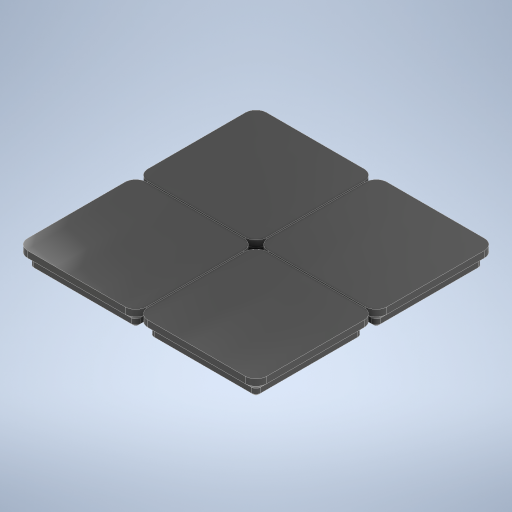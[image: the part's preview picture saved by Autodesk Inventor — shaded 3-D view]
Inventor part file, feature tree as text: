
AUTODESK INVENTOR PART (.ipt)
format: ipt  version: 2023 (Build 270158030, 158C)  size: 410,112 bytes
history: native  units: mm
features: extrude x6, sketch x6, projected_geometry x3, pattern_linear x1
ambient origin geometry x8: Origin, YZ Plane, XZ Plane, XY Plane, X Axis, Y Axis, Z Axis, Center Point
bodies: Solid2 (feature_tree)
feature tree (16):
  extrude  "base-generic"  Depth=41.5mm
  extrude  "Extrusion8"  Depth=3.75mm TaperAngle=0.0deg
  extrude  "Extrusion9"  Depth=2.15mm
  extrude  "Extrusion10"  Depth=0.8mm
  extrude  "Extrusion11"  Depth=7.75mm
  extrude  "Extrusion12"  Depth=0.5mm
  pattern_linear  "Rectangular Pattern1"  Spacing1=7.75mm  [1 undecoded]
  sketch  "Sketch9"  dims[d50=41.5mm d51=41.5mm]
  sketch  "Sketch10"  dims[d52=3.75mm d53=2.25mm d54=0.0mm]
  projected_geometry  "Projected Loop2"
  sketch  "Sketch11"  dims[d55=3.75mm d56=2.15mm d57=-7.853982mm]
  projected_geometry  "Projected Loop3"
  sketch  "Sketch12"  dims[d58=1.8mm d59=0.0mm d60=0.8mm d61=-7.853982mm]
  projected_geometry  "Projected Loop4"
  sketch  "Sketch13"  dims[d62=6.5mm d63=7.75mm]
  sketch  "Sketch14"  dims[d64=7.75mm d65=7.75mm d66=7.75mm d67=2.4mm d68=0.0mm d69=3.0mm d70=6.0mm d71=0.0mm d72=20.0mm d74=42.0mm d75=20.0mm d77=42.0mm d17=0.5mm d18=0.872665mm d19=0.5mm d20=0.872665mm d24=0.0mm d25=0.0mm d26=0.0mm d27=0.0mm]
note: 1 required parameter value undecoded (feature->parameter linkage not recoverable at this tier; creation-order binding heuristic only, values carry confidence <= 0.55)
